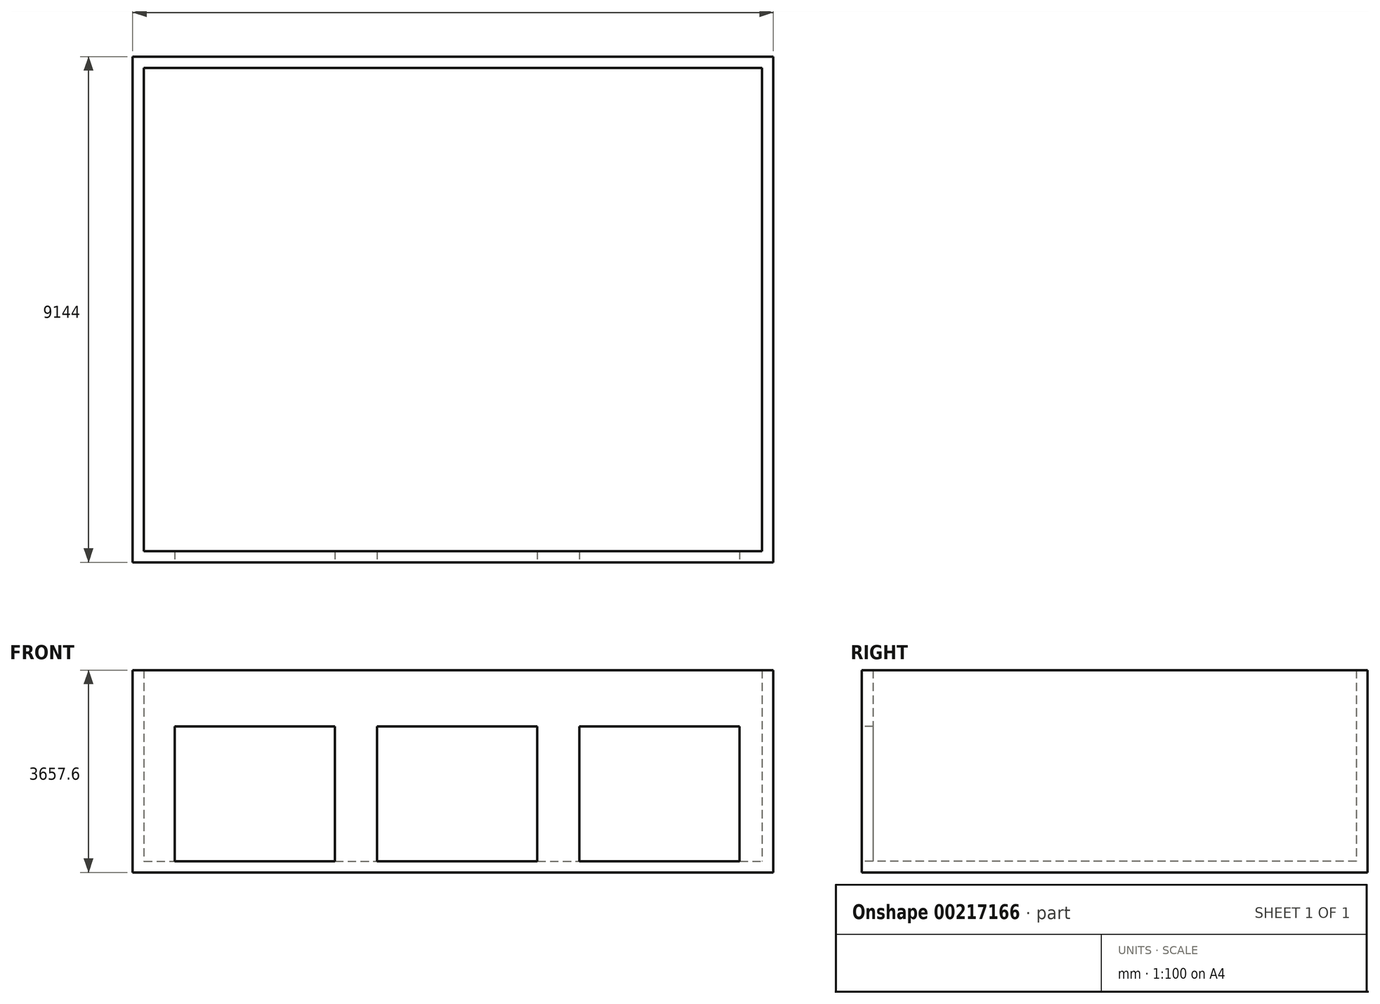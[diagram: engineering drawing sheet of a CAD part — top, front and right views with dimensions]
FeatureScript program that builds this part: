
annotation { "Feature Type Name" : "Feature", "Feature Type Description" : "" }
export const myFeature = defineFeature(function(context is Context, id is Id, definition is map)
    precondition{}
    {
        {
            var Q0;
            Q0=qCreatedBy(makeId("Top.planeOp"),FACE);
            var sketch = newSketch(context, id + "F0", { "sketchPlane" : qUnion([Q0])});
            skLineSegment(sketch, "E0.bottom", {"start": v(0, 0) * mm, "end": v(11582.4, 0) * mm});
            skLineSegment(sketch, "E0.top", {"start": v(0, -9144) * mm, "end": v(11582.4, -9144) * mm});
            skLineSegment(sketch, "E0.left", {"start": v(0, 0) * mm, "end": v(0, -9144) * mm});
            skLineSegment(sketch, "E0.right", {"start": v(11582.4, 0) * mm, "end": v(11582.4, -9144) * mm});
            skSolve(sketch);
        }
        {
            var Q0;
            Q0 = qSketchRegion(id + "F0", true);
            extrude(context, id + "F1", {"entities" : qUnion([Q0]), "depth" : 3657.6 * mm});
        }
        {
            var Q0;
            Q0=makeQuery(id+"F1.opExtrude","CAP_FACE",FACE,{"disambiguationData":[OSD([sQuery(id+"F0.wireOp",EDGE,"E0.bottom"),sQuery(id+"F0.wireOp",EDGE,"E0.top"),sQuery(id+"F0.wireOp",EDGE,"E0.left"),sQuery(id+"F0.wireOp",EDGE,"E0.right")])],"isStart":false});
            shell(context, id + "F2", {"entities" : qUnion([Q0]), "thickness" : 203.2 * mm});
        }
        {
            var Q0;
            Q0=makeQuery(id+"F1.opExtrude","SWEPT_FACE",FACE,{"disambiguationData":[OSD([sQuery(id+"F0.wireOp",EDGE,"E0.top")])]});
            var sketch = newSketch(context, id + "F3", { "sketchPlane" : qUnion([Q0])});
            skLineSegment(sketch, "E1.bottom", {"start": v(762, 2641.6) * mm, "end": v(3657.6, 2641.6) * mm});
            skLineSegment(sketch, "E1.top", {"start": v(762, 203.2) * mm, "end": v(3657.6, 203.2) * mm});
            skLineSegment(sketch, "E1.left", {"start": v(762, 2641.6) * mm, "end": v(762, 203.2) * mm});
            skLineSegment(sketch, "E1.right", {"start": v(3657.6, 2641.6) * mm, "end": v(3657.6, 203.2) * mm});
            skLineSegment(sketch, "E2.bottom", {"start": v(4419.6, 2641.6) * mm, "end": v(7315.2, 2641.6) * mm});
            skLineSegment(sketch, "E2.top", {"start": v(4419.6, 203.2) * mm, "end": v(7315.2, 203.2) * mm});
            skLineSegment(sketch, "E2.left", {"start": v(4419.6, 2641.6) * mm, "end": v(4419.6, 203.2) * mm});
            skLineSegment(sketch, "E2.right", {"start": v(7315.2, 2641.6) * mm, "end": v(7315.2, 203.2) * mm});
            skLineSegment(sketch, "E3.bottom", {"start": v(8077.2, 2641.6) * mm, "end": v(10972.8, 2641.6) * mm});
            skLineSegment(sketch, "E3.top", {"start": v(8077.2, 203.2) * mm, "end": v(10972.8, 203.2) * mm});
            skLineSegment(sketch, "E3.left", {"start": v(8077.2, 2641.6) * mm, "end": v(8077.2, 203.2) * mm});
            skLineSegment(sketch, "E3.right", {"start": v(10972.8, 2641.6) * mm, "end": v(10972.8, 203.2) * mm});
            skLineSegment(sketch, "E4", {"start": v(0, 203.2) * mm, "end": v(11582.4, 203.2) * mm, "construction": true});
            skSolve(sketch);
        }
        {
            var Q0;
            Q0 = qSketchRegion(id + "F3", true);
            var Q1;
            Q1=makeQuery(id+"F2.opShell","OFFSET_FACE",FACE,{"disambiguationData":[OSD([sQuery(id+"F0.wireOp",EDGE,"E0.top")])]});
            extrude(context, id + "F4", {"entities" : qUnion([Q0]), "operationType" : NewBodyOperationType.REMOVE, "endBound" : BoundingType.UP_TO_SURFACE, "oppositeDirection" : true, "endBoundEntityFace" : qUnion([Q1]), "depth" : 25.4 * mm});
        }
    });
